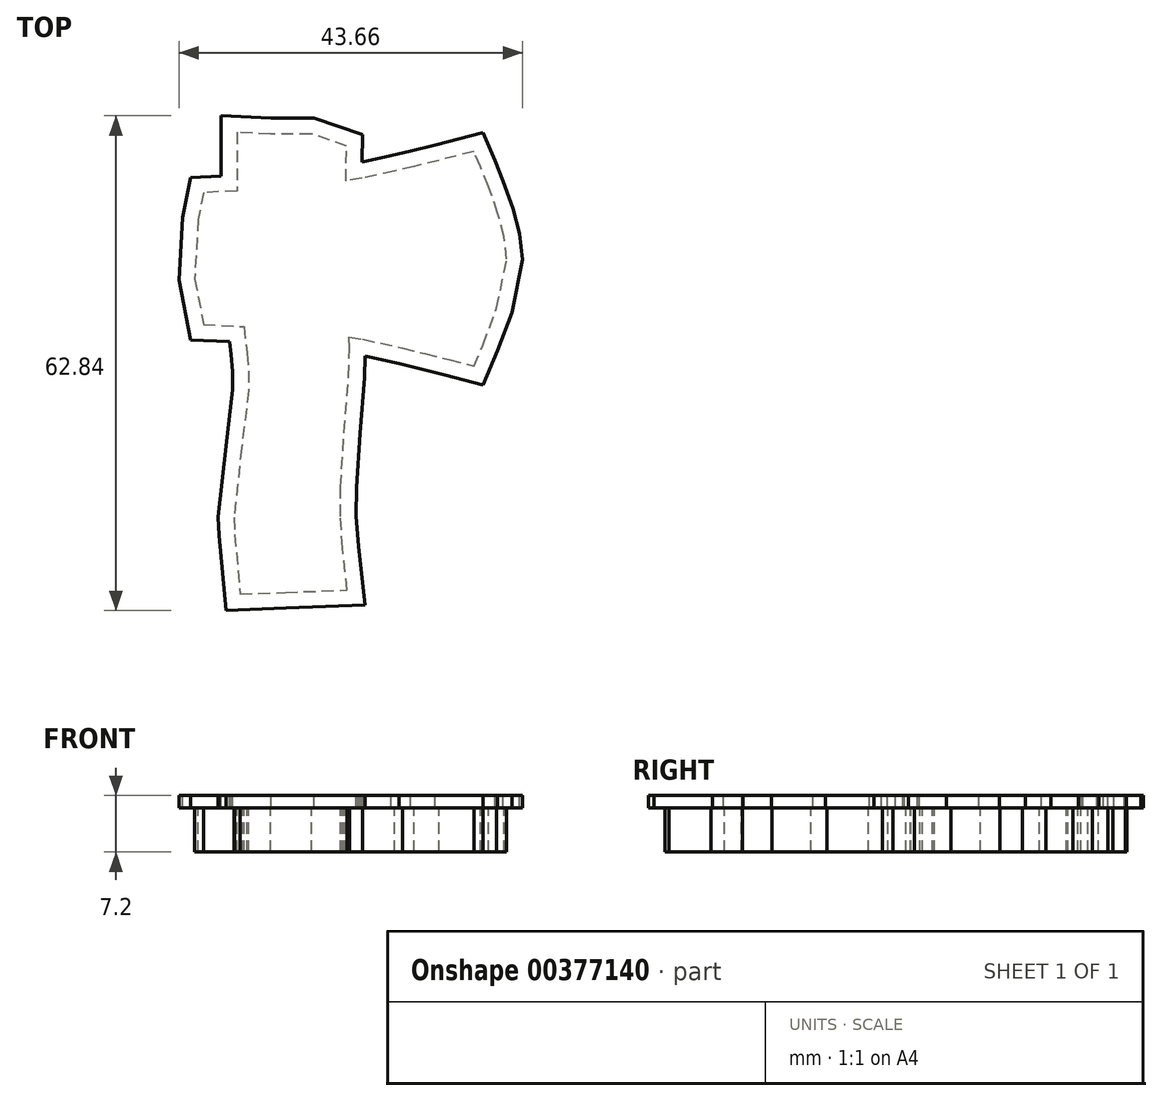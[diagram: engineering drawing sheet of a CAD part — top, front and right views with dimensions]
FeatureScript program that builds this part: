
annotation { "Feature Type Name" : "Feature", "Feature Type Description" : "" }
export const myFeature = defineFeature(function(context is Context, id is Id, definition is map)
    precondition{}
    {
        {
            var Q0;
            Q0=qCreatedBy(makeId("Top.planeOp"),FACE);
            var sketch = newSketch(context, id + "F0", { "sketchPlane" : qUnion([Q0])});
            skLineSegment(sketch, "E0", {"start": v(-5, 5.8) * mm, "end": v(-3.54, 5.88) * mm});
            skLineSegment(sketch, "E1", {"start": v(-3.54, 5.88) * mm, "end": v(-2.42, 5.96) * mm});
            skLineSegment(sketch, "E2", {"start": v(-2.42, 5.96) * mm, "end": v(-1.3, 6.05) * mm});
            skLineSegment(sketch, "E3", {"start": v(-1.3, 6.05) * mm, "end": v(-0.4, 6.16) * mm});
            skLineSegment(sketch, "E4", {"start": v(-0.4, 6.16) * mm, "end": v(0.44, 6.31) * mm});
            skLineSegment(sketch, "E5", {"start": v(0.44, 6.31) * mm, "end": v(1.6, 6.56) * mm});
            skLineSegment(sketch, "E6", {"start": v(1.6, 6.56) * mm, "end": v(2.29, 6.73) * mm});
            skLineSegment(sketch, "E7", {"start": v(2.29, 6.73) * mm, "end": v(3.16, 6.94) * mm});
            skLineSegment(sketch, "E8", {"start": v(3.16, 6.94) * mm, "end": v(4.22, 7.22) * mm});
            skLineSegment(sketch, "E9", {"start": v(4.22, 7.22) * mm, "end": v(4.37, 6.86) * mm});
            skLineSegment(sketch, "E10", {"start": v(4.37, 6.86) * mm, "end": v(4.65, 6.16) * mm});
            skLineSegment(sketch, "E11", {"start": v(4.65, 6.16) * mm, "end": v(4.98, 5.24) * mm});
            skLineSegment(sketch, "E12", {"start": v(4.98, 5.24) * mm, "end": v(5.2, 4.43) * mm});
            skLineSegment(sketch, "E13", {"start": v(5.2, 4.43) * mm, "end": v(5.28, 3.69) * mm});
            skLineSegment(sketch, "E14", {"start": v(5.28, 3.69) * mm, "end": v(4.94, 2) * mm});
            skLineSegment(sketch, "E15", {"start": v(4.94, 2) * mm, "end": v(4.46, 0.74) * mm});
            skLineSegment(sketch, "E16", {"start": v(4.46, 0.74) * mm, "end": v(4.22, 0.16) * mm});
            skLineSegment(sketch, "E17", {"start": v(4.22, 0.16) * mm, "end": v(3.52, 0.34) * mm});
            skLineSegment(sketch, "E18", {"start": v(3.52, 0.34) * mm, "end": v(2.67, 0.56) * mm});
            skLineSegment(sketch, "E19", {"start": v(2.67, 0.56) * mm, "end": v(1.88, 0.75) * mm});
            skLineSegment(sketch, "E20", {"start": v(1.88, 0.75) * mm, "end": v(0.47, 1.06) * mm});
            skLineSegment(sketch, "E21", {"start": v(0.47, 1.06) * mm, "end": v(-0.4, 1.22) * mm});
            skLineSegment(sketch, "E22", {"start": v(-0.4, 1.22) * mm, "end": v(-1.25, 1.33) * mm});
            skLineSegment(sketch, "E23", {"start": v(-1.25, 1.33) * mm, "end": v(-1.92, 1.4) * mm});
            skLineSegment(sketch, "E24", {"start": v(-1.92, 1.4) * mm, "end": v(-2.83, 1.46) * mm});
            skLineSegment(sketch, "E25", {"start": v(-2.83, 1.46) * mm, "end": v(-3.8, 1.52) * mm});
            skLineSegment(sketch, "E26", {"start": v(-3.8, 1.52) * mm, "end": v(-5, 1.58) * mm});
            skLineSegment(sketch, "E27", {"start": v(-5, 1.58) * mm, "end": v(-5.28, 3) * mm});
            skLineSegment(sketch, "E28", {"start": v(-5.28, 3) * mm, "end": v(-5.17, 5.05) * mm});
            skLineSegment(sketch, "E29", {"start": v(-5.17, 5.05) * mm, "end": v(-5, 5.8) * mm});
            skLineSegment(sketch, "E30", {"start": v(-5, 5.8) * mm, "end": v(-5, 5.8) * mm});
            skLineSegment(sketch, "E31", {"start": v(2.86, 0.52) * mm, "end": v(2.86, 1.93) * mm});
            skLineSegment(sketch, "E32", {"start": v(2.86, 1.93) * mm, "end": v(3.16, 3.33) * mm});
            skLineSegment(sketch, "E33", {"start": v(3.16, 3.33) * mm, "end": v(2.86, 4.4) * mm});
            skLineSegment(sketch, "E34", {"start": v(2.86, 4.4) * mm, "end": v(2.86, 6.86) * mm});
            skLineSegment(sketch, "E35", {"start": v(-3.8, 5.87) * mm, "end": v(-3.8, 7.92) * mm});
            skLineSegment(sketch, "E36", {"start": v(-3.8, 7.92) * mm, "end": v(-2.83, 7.87) * mm});
            skLineSegment(sketch, "E37", {"start": v(-2.83, 7.87) * mm, "end": v(-1.42, 7.87) * mm});
            skLineSegment(sketch, "E38", {"start": v(-1.42, 7.87) * mm, "end": v(-0.37, 7.51) * mm});
            skLineSegment(sketch, "E39", {"start": v(-0.37, 7.51) * mm, "end": v(-0.4, 6.16) * mm});
            skLineSegment(sketch, "E40", {"start": v(-0.28, 1.2) * mm, "end": v(-0.27, 0.52) * mm});
            skLineSegment(sketch, "E41", {"start": v(-0.27, 0.52) * mm, "end": v(-0.29, -0.46) * mm});
            skLineSegment(sketch, "E42", {"start": v(-0.29, -0.46) * mm, "end": v(-0.45, -2.42) * mm});
            skLineSegment(sketch, "E43", {"start": v(-0.45, -2.42) * mm, "end": v(-0.58, -4.36) * mm});
            skLineSegment(sketch, "E44", {"start": v(-0.58, -4.36) * mm, "end": v(-0.59, -5.4) * mm});
            skLineSegment(sketch, "E45", {"start": v(-0.59, -5.4) * mm, "end": v(-0.5, -6.53) * mm});
            skLineSegment(sketch, "E46", {"start": v(-0.5, -6.53) * mm, "end": v(-0.37, -7.79) * mm});
            skLineSegment(sketch, "E47", {"start": v(-0.37, -7.79) * mm, "end": v(-2.3, -7.86) * mm});
            skLineSegment(sketch, "E48", {"start": v(-2.3, -7.86) * mm, "end": v(-3.7, -7.92) * mm});
            skLineSegment(sketch, "E49", {"start": v(-3.7, -7.92) * mm, "end": v(-3.87, -6.03) * mm});
            skLineSegment(sketch, "E50", {"start": v(-3.87, -6.03) * mm, "end": v(-3.9, -5.45) * mm});
            skLineSegment(sketch, "E51", {"start": v(-3.9, -5.45) * mm, "end": v(-3.63, -3.01) * mm});
            skLineSegment(sketch, "E52", {"start": v(-3.63, -3.01) * mm, "end": v(-3.38, -0.98) * mm});
            skLineSegment(sketch, "E53", {"start": v(-3.38, -0.98) * mm, "end": v(-3.39, -0.26) * mm});
            skLineSegment(sketch, "E54", {"start": v(-3.39, -0.26) * mm, "end": v(-3.44, 0.38) * mm});
            skLineSegment(sketch, "E55", {"start": v(-3.44, 0.38) * mm, "end": v(-3.57, 1.5) * mm});
            skSolve(sketch);
        }
        {
            var Q0;
            {var subQ8=sQuery(id+"F0.wireOp",EDGE,"E22");Q0=makeQuery(id+"F0.imprint","IMPRINT",FACE,{"disambiguationData":[TD([[makeQuery(id+"F0.imprint","IMPRINT",EDGE,{"derivedFrom":subQ8}),1.0]])]});}
            var Q1;
            {var subQ1=sQuery(id+"F0.wireOp",EDGE,"E1");Q1=makeQuery(id+"F0.imprint","IMPRINT",FACE,{"disambiguationData":[TD([[makeQuery(id+"F0.imprint","IMPRINT",EDGE,{"derivedFrom":subQ1}),-1.0]])]});}
            var Q2;
            {var subQ0=sQuery(id+"F0.wireOp",EDGE,"E1");Q2=makeQuery(id+"F0.imprint","IMPRINT",FACE,{"disambiguationData":[TD([[makeQuery(id+"F0.imprint","IMPRINT",EDGE,{"derivedFrom":subQ0}),1.0]])]});}
            extrude(context, id + "F1", {"entities" : qUnion([Q0, Q1, Q2]), "depth" : 2 * mm});
        }
        {
            var Q0;
            Q0=makeQuery(id+"F1.opExtrude","SWEPT_BODY",BODY,{"disambiguationData":[OSD([sQuery(id+"F0.wireOp",EDGE,"E0"),sQuery(id+"F0.wireOp",EDGE,"E4"),sQuery(id+"F0.wireOp",EDGE,"E5"),sQuery(id+"F0.wireOp",EDGE,"E6"),sQuery(id+"F0.wireOp",EDGE,"E7"),sQuery(id+"F0.wireOp",EDGE,"E8"),sQuery(id+"F0.wireOp",EDGE,"E9"),sQuery(id+"F0.wireOp",EDGE,"E10"),sQuery(id+"F0.wireOp",EDGE,"E11"),sQuery(id+"F0.wireOp",EDGE,"E12"),sQuery(id+"F0.wireOp",EDGE,"E13"),sQuery(id+"F0.wireOp",EDGE,"E14"),sQuery(id+"F0.wireOp",EDGE,"E15"),sQuery(id+"F0.wireOp",EDGE,"E16"),sQuery(id+"F0.wireOp",EDGE,"E17"),sQuery(id+"F0.wireOp",EDGE,"E18"),sQuery(id+"F0.wireOp",EDGE,"E19"),sQuery(id+"F0.wireOp",EDGE,"E20"),sQuery(id+"F0.wireOp",EDGE,"E21"),sQuery(id+"F0.wireOp",EDGE,"E25"),sQuery(id+"F0.wireOp",EDGE,"E26"),sQuery(id+"F0.wireOp",EDGE,"E27"),sQuery(id+"F0.wireOp",EDGE,"E28"),sQuery(id+"F0.wireOp",EDGE,"E29"),sQuery(id+"F0.wireOp",EDGE,"E35"),sQuery(id+"F0.wireOp",EDGE,"E36"),sQuery(id+"F0.wireOp",EDGE,"E37"),sQuery(id+"F0.wireOp",EDGE,"E38"),sQuery(id+"F0.wireOp",EDGE,"E39"),sQuery(id+"F0.wireOp",EDGE,"E40"),sQuery(id+"F0.wireOp",EDGE,"E41"),sQuery(id+"F0.wireOp",EDGE,"E42"),sQuery(id+"F0.wireOp",EDGE,"E43"),sQuery(id+"F0.wireOp",EDGE,"E44"),sQuery(id+"F0.wireOp",EDGE,"E45"),sQuery(id+"F0.wireOp",EDGE,"E46"),sQuery(id+"F0.wireOp",EDGE,"E47"),sQuery(id+"F0.wireOp",EDGE,"E48"),sQuery(id+"F0.wireOp",EDGE,"E49"),sQuery(id+"F0.wireOp",EDGE,"E50"),sQuery(id+"F0.wireOp",EDGE,"E51"),sQuery(id+"F0.wireOp",EDGE,"E52"),sQuery(id+"F0.wireOp",EDGE,"E53"),sQuery(id+"F0.wireOp",EDGE,"E54"),sQuery(id+"F0.wireOp",EDGE,"E55")])]});
            var Q1;
            Q1=qCreatedBy(makeId("Origin.pointOp"),VERTEX);
            transform(context, id + "F2", {"entities" : qUnion([Q0]), "transformType" : TransformType.SCALE_UNIFORMLY, "scale" : 3.6, "scalePoint" : qUnion([Q1]), "makeCopy" : false});
        }
        {
            var Q0;
            Q0=makeQuery(id+"F1.opExtrude","CAP_FACE",FACE,{"disambiguationData":[OSD([sQuery(id+"F0.wireOp",EDGE,"E0"),sQuery(id+"F0.wireOp",EDGE,"E4"),sQuery(id+"F0.wireOp",EDGE,"E5"),sQuery(id+"F0.wireOp",EDGE,"E6"),sQuery(id+"F0.wireOp",EDGE,"E7"),sQuery(id+"F0.wireOp",EDGE,"E8"),sQuery(id+"F0.wireOp",EDGE,"E9"),sQuery(id+"F0.wireOp",EDGE,"E10"),sQuery(id+"F0.wireOp",EDGE,"E11"),sQuery(id+"F0.wireOp",EDGE,"E12"),sQuery(id+"F0.wireOp",EDGE,"E13"),sQuery(id+"F0.wireOp",EDGE,"E14"),sQuery(id+"F0.wireOp",EDGE,"E15"),sQuery(id+"F0.wireOp",EDGE,"E16"),sQuery(id+"F0.wireOp",EDGE,"E17"),sQuery(id+"F0.wireOp",EDGE,"E18"),sQuery(id+"F0.wireOp",EDGE,"E19"),sQuery(id+"F0.wireOp",EDGE,"E20"),sQuery(id+"F0.wireOp",EDGE,"E21"),sQuery(id+"F0.wireOp",EDGE,"E25"),sQuery(id+"F0.wireOp",EDGE,"E26"),sQuery(id+"F0.wireOp",EDGE,"E27"),sQuery(id+"F0.wireOp",EDGE,"E28"),sQuery(id+"F0.wireOp",EDGE,"E29"),sQuery(id+"F0.wireOp",EDGE,"E35"),sQuery(id+"F0.wireOp",EDGE,"E36"),sQuery(id+"F0.wireOp",EDGE,"E37"),sQuery(id+"F0.wireOp",EDGE,"E38"),sQuery(id+"F0.wireOp",EDGE,"E39"),sQuery(id+"F0.wireOp",EDGE,"E40"),sQuery(id+"F0.wireOp",EDGE,"E41"),sQuery(id+"F0.wireOp",EDGE,"E42"),sQuery(id+"F0.wireOp",EDGE,"E43"),sQuery(id+"F0.wireOp",EDGE,"E44"),sQuery(id+"F0.wireOp",EDGE,"E45"),sQuery(id+"F0.wireOp",EDGE,"E46"),sQuery(id+"F0.wireOp",EDGE,"E47"),sQuery(id+"F0.wireOp",EDGE,"E48"),sQuery(id+"F0.wireOp",EDGE,"E49"),sQuery(id+"F0.wireOp",EDGE,"E50"),sQuery(id+"F0.wireOp",EDGE,"E51"),sQuery(id+"F0.wireOp",EDGE,"E52"),sQuery(id+"F0.wireOp",EDGE,"E53"),sQuery(id+"F0.wireOp",EDGE,"E54"),sQuery(id+"F0.wireOp",EDGE,"E55")])],"isStart":false});
            var sketch = newSketch(context, id + "F3", { "sketchPlane" : qUnion([Q0])});
            skLineSegment(sketch, "E56.0", {"start": v(-18.7, 4.9) * mm, "end": v(-13.7, 4.66) * mm});
            skLineSegment(sketch, "E56.1", {"start": v(-19.81, 10.72) * mm, "end": v(-18.7, 4.9) * mm});
            skLineSegment(sketch, "E56.2", {"start": v(-19.4, 18.27) * mm, "end": v(-19.81, 10.72) * mm});
            skLineSegment(sketch, "E56.3", {"start": v(-18.69, 21.68) * mm, "end": v(-19.4, 18.27) * mm});
            skLineSegment(sketch, "E56.4", {"start": v(-14.46, 21.9) * mm, "end": v(-18.69, 21.68) * mm});
            skLineSegment(sketch, "E56.5", {"start": v(-14.46, 29.34) * mm, "end": v(-14.46, 21.9) * mm});
            skLineSegment(sketch, "E56.6", {"start": v(-10.18, 29.13) * mm, "end": v(-14.46, 29.34) * mm});
            skLineSegment(sketch, "E56.7", {"start": v(-4.99, 29.13) * mm, "end": v(-10.18, 29.13) * mm});
            skLineSegment(sketch, "E56.8", {"start": v(-0.52, 27.6) * mm, "end": v(-4.99, 29.13) * mm});
            skLineSegment(sketch, "E56.9", {"start": v(-0.6, 23.14) * mm, "end": v(-0.52, 27.6) * mm});
            skLineSegment(sketch, "E56.10", {"start": v(1.42, 23.5) * mm, "end": v(-0.6, 23.14) * mm});
            skLineSegment(sketch, "E56.11", {"start": v(-13.7, 4.66) * mm, "end": v(-13.56, 4.65) * mm});
            skLineSegment(sketch, "E56.12", {"start": v(5.56, 24.4) * mm, "end": v(1.42, 23.5) * mm});
            skLineSegment(sketch, "E56.13", {"start": v(8.04, 25) * mm, "end": v(5.56, 24.4) * mm});
            skLineSegment(sketch, "E56.14", {"start": v(11.2, 25.77) * mm, "end": v(8.04, 25) * mm});
            skLineSegment(sketch, "E56.15", {"start": v(15.64, 26.92) * mm, "end": v(11.2, 25.77) * mm});
            skLineSegment(sketch, "E56.16", {"start": v(16.48, 25) * mm, "end": v(15.64, 26.92) * mm});
            skLineSegment(sketch, "E56.17", {"start": v(17.5, 22.47) * mm, "end": v(16.48, 25) * mm});
            skLineSegment(sketch, "E56.18", {"start": v(18.68, 19.1) * mm, "end": v(17.5, 22.47) * mm});
            skLineSegment(sketch, "E56.19", {"start": v(19.47, 16.1) * mm, "end": v(18.68, 19.1) * mm});
            skLineSegment(sketch, "E56.20", {"start": v(19.82, 13.24) * mm, "end": v(19.47, 16.1) * mm});
            skLineSegment(sketch, "E56.21", {"start": v(18.54, 7) * mm, "end": v(19.82, 13.24) * mm});
            skLineSegment(sketch, "E56.22", {"start": v(16.82, 2.35) * mm, "end": v(18.54, 7) * mm});
            skLineSegment(sketch, "E56.23", {"start": v(-0.43, -28.8) * mm, "end": v(-1.03, -23.45) * mm});
            skLineSegment(sketch, "E56.24", {"start": v(-8.28, -29.1) * mm, "end": v(-0.43, -28.8) * mm});
            skLineSegment(sketch, "E56.25", {"start": v(-14.03, -29.33) * mm, "end": v(-8.28, -29.1) * mm});
            skLineSegment(sketch, "E56.26", {"start": v(-14.73, -21.77) * mm, "end": v(-14.03, -29.33) * mm});
            skLineSegment(sketch, "E56.27", {"start": v(-14.81, -19.6) * mm, "end": v(-14.73, -21.77) * mm});
            skLineSegment(sketch, "E56.28", {"start": v(-13.86, -10.75) * mm, "end": v(-14.81, -19.6) * mm});
            skLineSegment(sketch, "E56.29", {"start": v(-13.56, 4.65) * mm, "end": v(-13.19, 1.3) * mm});
            skLineSegment(sketch, "E56.30", {"start": v(-13.19, 1.3) * mm, "end": v(-13, -0.98) * mm});
            skLineSegment(sketch, "E56.31", {"start": v(-13, -0.98) * mm, "end": v(-12.98, -3.47) * mm});
            skLineSegment(sketch, "E56.32", {"start": v(-12.98, -3.47) * mm, "end": v(-13.86, -10.75) * mm});
            skLineSegment(sketch, "E56.33", {"start": v(-1.03, -23.45) * mm, "end": v(-1.31, -19.45) * mm});
            skLineSegment(sketch, "E56.34", {"start": v(-1.31, -19.45) * mm, "end": v(-1.28, -15.72) * mm});
            skLineSegment(sketch, "E56.35", {"start": v(-1.28, -15.72) * mm, "end": v(-0.82, -8.77) * mm});
            skLineSegment(sketch, "E56.36", {"start": v(-0.82, -8.77) * mm, "end": v(-0.24, -1.7) * mm});
            skLineSegment(sketch, "E56.37", {"start": v(-0.24, -1.7) * mm, "end": v(-0.17, 1.86) * mm});
            skLineSegment(sketch, "E56.38", {"start": v(-0.17, 1.86) * mm, "end": v(-0.18, 3.36) * mm});
            skLineSegment(sketch, "E56.39", {"start": v(-0.18, 3.36) * mm, "end": v(1.54, 3.05) * mm});
            skLineSegment(sketch, "E56.40", {"start": v(1.54, 3.05) * mm, "end": v(6.6, 1.92) * mm});
            skLineSegment(sketch, "E56.41", {"start": v(6.6, 1.92) * mm, "end": v(9.43, 1.23) * mm});
            skLineSegment(sketch, "E56.42", {"start": v(9.43, 1.23) * mm, "end": v(12.47, 0.46) * mm});
            skLineSegment(sketch, "E56.43", {"start": v(12.47, 0.46) * mm, "end": v(15.64, -0.37) * mm});
            skLineSegment(sketch, "E56.44", {"start": v(15.64, -0.37) * mm, "end": v(16.82, 2.35) * mm});
            skSolve(sketch);
        }
        {
            var Q0;
            Q0=makeQuery(id+"F3.imprint","IMPRINT",FACE,{"disambiguationData":[TD([[makeQuery(id+"F3.imprint","IMPRINT",EDGE,{"derivedFrom":sQuery(id+"F3.wireOp",EDGE,"E56.0")}),1.0]])]});
            var Q1;
            Q1=makeQuery(id+"F1.opExtrude","CAP_FACE",FACE,{"disambiguationData":[OSD([sQuery(id+"F0.wireOp",EDGE,"E0"),sQuery(id+"F0.wireOp",EDGE,"E4"),sQuery(id+"F0.wireOp",EDGE,"E5"),sQuery(id+"F0.wireOp",EDGE,"E6"),sQuery(id+"F0.wireOp",EDGE,"E7"),sQuery(id+"F0.wireOp",EDGE,"E8"),sQuery(id+"F0.wireOp",EDGE,"E9"),sQuery(id+"F0.wireOp",EDGE,"E10"),sQuery(id+"F0.wireOp",EDGE,"E11"),sQuery(id+"F0.wireOp",EDGE,"E12"),sQuery(id+"F0.wireOp",EDGE,"E13"),sQuery(id+"F0.wireOp",EDGE,"E14"),sQuery(id+"F0.wireOp",EDGE,"E15"),sQuery(id+"F0.wireOp",EDGE,"E16"),sQuery(id+"F0.wireOp",EDGE,"E17"),sQuery(id+"F0.wireOp",EDGE,"E18"),sQuery(id+"F0.wireOp",EDGE,"E19"),sQuery(id+"F0.wireOp",EDGE,"E20"),sQuery(id+"F0.wireOp",EDGE,"E21"),sQuery(id+"F0.wireOp",EDGE,"E25"),sQuery(id+"F0.wireOp",EDGE,"E26"),sQuery(id+"F0.wireOp",EDGE,"E27"),sQuery(id+"F0.wireOp",EDGE,"E28"),sQuery(id+"F0.wireOp",EDGE,"E29"),sQuery(id+"F0.wireOp",EDGE,"E35"),sQuery(id+"F0.wireOp",EDGE,"E36"),sQuery(id+"F0.wireOp",EDGE,"E37"),sQuery(id+"F0.wireOp",EDGE,"E38"),sQuery(id+"F0.wireOp",EDGE,"E39"),sQuery(id+"F0.wireOp",EDGE,"E40"),sQuery(id+"F0.wireOp",EDGE,"E41"),sQuery(id+"F0.wireOp",EDGE,"E42"),sQuery(id+"F0.wireOp",EDGE,"E43"),sQuery(id+"F0.wireOp",EDGE,"E44"),sQuery(id+"F0.wireOp",EDGE,"E45"),sQuery(id+"F0.wireOp",EDGE,"E46"),sQuery(id+"F0.wireOp",EDGE,"E47"),sQuery(id+"F0.wireOp",EDGE,"E48"),sQuery(id+"F0.wireOp",EDGE,"E49"),sQuery(id+"F0.wireOp",EDGE,"E50"),sQuery(id+"F0.wireOp",EDGE,"E51"),sQuery(id+"F0.wireOp",EDGE,"E52"),sQuery(id+"F0.wireOp",EDGE,"E53"),sQuery(id+"F0.wireOp",EDGE,"E54"),sQuery(id+"F0.wireOp",EDGE,"E55")])],"isStart":true});
            extrude(context, id + "F4", {"entities" : qUnion([Q0]), "endBound" : BoundingType.UP_TO_SURFACE, "oppositeDirection" : true, "endBoundEntityFace" : qUnion([Q1]), "depth" : 5 * mm});
        }
        {
            var Q0;
            Q0=makeQuery(id+"F4.opExtrude","CAP_FACE",FACE,{"disambiguationData":[OSD([sQuery(id+"F0.wireOp",EDGE,"E0"),sQuery(id+"F0.wireOp",EDGE,"E4"),sQuery(id+"F0.wireOp",EDGE,"E5"),sQuery(id+"F0.wireOp",EDGE,"E6"),sQuery(id+"F0.wireOp",EDGE,"E7"),sQuery(id+"F0.wireOp",EDGE,"E8"),sQuery(id+"F0.wireOp",EDGE,"E9"),sQuery(id+"F0.wireOp",EDGE,"E10"),sQuery(id+"F0.wireOp",EDGE,"E11"),sQuery(id+"F0.wireOp",EDGE,"E12"),sQuery(id+"F0.wireOp",EDGE,"E13"),sQuery(id+"F0.wireOp",EDGE,"E14"),sQuery(id+"F0.wireOp",EDGE,"E15"),sQuery(id+"F0.wireOp",EDGE,"E16"),sQuery(id+"F0.wireOp",EDGE,"E17"),sQuery(id+"F0.wireOp",EDGE,"E18"),sQuery(id+"F0.wireOp",EDGE,"E19"),sQuery(id+"F0.wireOp",EDGE,"E20"),sQuery(id+"F0.wireOp",EDGE,"E21"),sQuery(id+"F0.wireOp",EDGE,"E25"),sQuery(id+"F0.wireOp",EDGE,"E26"),sQuery(id+"F0.wireOp",EDGE,"E27"),sQuery(id+"F0.wireOp",EDGE,"E28"),sQuery(id+"F0.wireOp",EDGE,"E29"),sQuery(id+"F0.wireOp",EDGE,"E35"),sQuery(id+"F0.wireOp",EDGE,"E36"),sQuery(id+"F0.wireOp",EDGE,"E37"),sQuery(id+"F0.wireOp",EDGE,"E38"),sQuery(id+"F0.wireOp",EDGE,"E39"),sQuery(id+"F0.wireOp",EDGE,"E40"),sQuery(id+"F0.wireOp",EDGE,"E41"),sQuery(id+"F0.wireOp",EDGE,"E42"),sQuery(id+"F0.wireOp",EDGE,"E43"),sQuery(id+"F0.wireOp",EDGE,"E44"),sQuery(id+"F0.wireOp",EDGE,"E45"),sQuery(id+"F0.wireOp",EDGE,"E46"),sQuery(id+"F0.wireOp",EDGE,"E47"),sQuery(id+"F0.wireOp",EDGE,"E48"),sQuery(id+"F0.wireOp",EDGE,"E49"),sQuery(id+"F0.wireOp",EDGE,"E50"),sQuery(id+"F0.wireOp",EDGE,"E51"),sQuery(id+"F0.wireOp",EDGE,"E52"),sQuery(id+"F0.wireOp",EDGE,"E53"),sQuery(id+"F0.wireOp",EDGE,"E54"),sQuery(id+"F0.wireOp",EDGE,"E55"),sQuery(id+"F3.wireOp",EDGE,"E56.0"),sQuery(id+"F3.wireOp",EDGE,"E56.1"),sQuery(id+"F3.wireOp",EDGE,"E56.2"),sQuery(id+"F3.wireOp",EDGE,"E56.3"),sQuery(id+"F3.wireOp",EDGE,"E56.4"),sQuery(id+"F3.wireOp",EDGE,"E56.5"),sQuery(id+"F3.wireOp",EDGE,"E56.6"),sQuery(id+"F3.wireOp",EDGE,"E56.7"),sQuery(id+"F3.wireOp",EDGE,"E56.8"),sQuery(id+"F3.wireOp",EDGE,"E56.9"),sQuery(id+"F3.wireOp",EDGE,"E56.10"),sQuery(id+"F3.wireOp",EDGE,"E56.11"),sQuery(id+"F3.wireOp",EDGE,"E56.12"),sQuery(id+"F3.wireOp",EDGE,"E56.13"),sQuery(id+"F3.wireOp",EDGE,"E56.14"),sQuery(id+"F3.wireOp",EDGE,"E56.15"),sQuery(id+"F3.wireOp",EDGE,"E56.16"),sQuery(id+"F3.wireOp",EDGE,"E56.17"),sQuery(id+"F3.wireOp",EDGE,"E56.18"),sQuery(id+"F3.wireOp",EDGE,"E56.19"),sQuery(id+"F3.wireOp",EDGE,"E56.20"),sQuery(id+"F3.wireOp",EDGE,"E56.21"),sQuery(id+"F3.wireOp",EDGE,"E56.22"),sQuery(id+"F3.wireOp",EDGE,"E56.23"),sQuery(id+"F3.wireOp",EDGE,"E56.24"),sQuery(id+"F3.wireOp",EDGE,"E56.25"),sQuery(id+"F3.wireOp",EDGE,"E56.26"),sQuery(id+"F3.wireOp",EDGE,"E56.27"),sQuery(id+"F3.wireOp",EDGE,"E56.28"),sQuery(id+"F3.wireOp",EDGE,"E56.29"),sQuery(id+"F3.wireOp",EDGE,"E56.30"),sQuery(id+"F3.wireOp",EDGE,"E56.31"),sQuery(id+"F3.wireOp",EDGE,"E56.32"),sQuery(id+"F3.wireOp",EDGE,"E56.33"),sQuery(id+"F3.wireOp",EDGE,"E56.34"),sQuery(id+"F3.wireOp",EDGE,"E56.35"),sQuery(id+"F3.wireOp",EDGE,"E56.36"),sQuery(id+"F3.wireOp",EDGE,"E56.37"),sQuery(id+"F3.wireOp",EDGE,"E56.38"),sQuery(id+"F3.wireOp",EDGE,"E56.39"),sQuery(id+"F3.wireOp",EDGE,"E56.40"),sQuery(id+"F3.wireOp",EDGE,"E56.41"),sQuery(id+"F3.wireOp",EDGE,"E56.42"),sQuery(id+"F3.wireOp",EDGE,"E56.43"),sQuery(id+"F3.wireOp",EDGE,"E56.44")])],"isStart":true});
            var sketch = newSketch(context, id + "F5", { "sketchPlane" : qUnion([Q0])});
            skLineSegment(sketch, "E57", {"start": v(9.8, 24.6) * mm, "end": v(9.8, 13.66) * mm});
            skLineSegment(sketch, "E58", {"start": v(9.8, 13.66) * mm, "end": v(8.23, 11.38) * mm});
            skLineSegment(sketch, "E59", {"start": v(8.23, 11.38) * mm, "end": v(9.73, 7) * mm});
            skLineSegment(sketch, "E60", {"start": v(9.73, 7) * mm, "end": v(9.62, 2.01) * mm});
            skLineSegment(sketch, "E61.0", {"start": v(8.23, 24.22) * mm, "end": v(11.39, 25) * mm});
            skLineSegment(sketch, "E62.0", {"start": v(12.67, 1.24) * mm, "end": v(9.62, 2.01) * mm});
            skLineSegment(sketch, "E63.0", {"start": v(9.62, 2.01) * mm, "end": v(6.77, 2.7) * mm});
            skLineSegment(sketch, "E64.0", {"start": v(8.13, 6.76) * mm, "end": v(8.01, 1.8) * mm});
            skLineSegment(sketch, "E64.1", {"start": v(6.45, 11.63) * mm, "end": v(8.13, 6.76) * mm});
            skLineSegment(sketch, "E64.2", {"start": v(8.2, 14.16) * mm, "end": v(6.45, 11.63) * mm});
            skLineSegment(sketch, "E64.3", {"start": v(8.2, 24.6) * mm, "end": v(8.2, 14.16) * mm});
            skSolve(sketch);
        }
        {
            var Q0;
            {var subQ5=sQuery(id+"F5.wireOp",EDGE,"E57");Q0=makeQuery(id+"F5.imprint","IMPRINT",FACE,{"disambiguationData":[TD([[makeQuery(id+"F5.imprint","IMPRINT",EDGE,{"derivedFrom":subQ5}),-1.0]])]});}
            extrude(context, id + "F6", {"entities" : qUnion([Q0]), "operationType" : NewBodyOperationType.ADD, "oppositeDirection" : true, "depth" : 5 * mm});
        }
        {
            var Q0;
            Q0=makeQuery(id+"F6.boolean.opBoolean","MERGE",FACE,{"derivedFrom":[makeQuery(id+"F4.opExtrude","CAP_FACE",FACE,{"disambiguationData":[OSD([sQuery(id+"F0.wireOp",EDGE,"E0"),sQuery(id+"F0.wireOp",EDGE,"E4"),sQuery(id+"F0.wireOp",EDGE,"E5"),sQuery(id+"F0.wireOp",EDGE,"E6"),sQuery(id+"F0.wireOp",EDGE,"E7"),sQuery(id+"F0.wireOp",EDGE,"E8"),sQuery(id+"F0.wireOp",EDGE,"E9"),sQuery(id+"F0.wireOp",EDGE,"E10"),sQuery(id+"F0.wireOp",EDGE,"E11"),sQuery(id+"F0.wireOp",EDGE,"E12"),sQuery(id+"F0.wireOp",EDGE,"E13"),sQuery(id+"F0.wireOp",EDGE,"E14"),sQuery(id+"F0.wireOp",EDGE,"E15"),sQuery(id+"F0.wireOp",EDGE,"E16"),sQuery(id+"F0.wireOp",EDGE,"E17"),sQuery(id+"F0.wireOp",EDGE,"E18"),sQuery(id+"F0.wireOp",EDGE,"E19"),sQuery(id+"F0.wireOp",EDGE,"E20"),sQuery(id+"F0.wireOp",EDGE,"E21"),sQuery(id+"F0.wireOp",EDGE,"E25"),sQuery(id+"F0.wireOp",EDGE,"E26"),sQuery(id+"F0.wireOp",EDGE,"E27"),sQuery(id+"F0.wireOp",EDGE,"E28"),sQuery(id+"F0.wireOp",EDGE,"E29"),sQuery(id+"F0.wireOp",EDGE,"E35"),sQuery(id+"F0.wireOp",EDGE,"E36"),sQuery(id+"F0.wireOp",EDGE,"E37"),sQuery(id+"F0.wireOp",EDGE,"E38"),sQuery(id+"F0.wireOp",EDGE,"E39"),sQuery(id+"F0.wireOp",EDGE,"E40"),sQuery(id+"F0.wireOp",EDGE,"E41"),sQuery(id+"F0.wireOp",EDGE,"E42"),sQuery(id+"F0.wireOp",EDGE,"E43"),sQuery(id+"F0.wireOp",EDGE,"E44"),sQuery(id+"F0.wireOp",EDGE,"E45"),sQuery(id+"F0.wireOp",EDGE,"E46"),sQuery(id+"F0.wireOp",EDGE,"E47"),sQuery(id+"F0.wireOp",EDGE,"E48"),sQuery(id+"F0.wireOp",EDGE,"E49"),sQuery(id+"F0.wireOp",EDGE,"E50"),sQuery(id+"F0.wireOp",EDGE,"E51"),sQuery(id+"F0.wireOp",EDGE,"E52"),sQuery(id+"F0.wireOp",EDGE,"E53"),sQuery(id+"F0.wireOp",EDGE,"E54"),sQuery(id+"F0.wireOp",EDGE,"E55"),sQuery(id+"F3.wireOp",EDGE,"E56.0"),sQuery(id+"F3.wireOp",EDGE,"E56.1"),sQuery(id+"F3.wireOp",EDGE,"E56.2"),sQuery(id+"F3.wireOp",EDGE,"E56.3"),sQuery(id+"F3.wireOp",EDGE,"E56.4"),sQuery(id+"F3.wireOp",EDGE,"E56.5"),sQuery(id+"F3.wireOp",EDGE,"E56.6"),sQuery(id+"F3.wireOp",EDGE,"E56.7"),sQuery(id+"F3.wireOp",EDGE,"E56.8"),sQuery(id+"F3.wireOp",EDGE,"E56.9"),sQuery(id+"F3.wireOp",EDGE,"E56.10"),sQuery(id+"F3.wireOp",EDGE,"E56.11"),sQuery(id+"F3.wireOp",EDGE,"E56.12"),sQuery(id+"F3.wireOp",EDGE,"E56.13"),sQuery(id+"F3.wireOp",EDGE,"E56.14"),sQuery(id+"F3.wireOp",EDGE,"E56.15"),sQuery(id+"F3.wireOp",EDGE,"E56.16"),sQuery(id+"F3.wireOp",EDGE,"E56.17"),sQuery(id+"F3.wireOp",EDGE,"E56.18"),sQuery(id+"F3.wireOp",EDGE,"E56.19"),sQuery(id+"F3.wireOp",EDGE,"E56.20"),sQuery(id+"F3.wireOp",EDGE,"E56.21"),sQuery(id+"F3.wireOp",EDGE,"E56.22"),sQuery(id+"F3.wireOp",EDGE,"E56.23"),sQuery(id+"F3.wireOp",EDGE,"E56.24"),sQuery(id+"F3.wireOp",EDGE,"E56.25"),sQuery(id+"F3.wireOp",EDGE,"E56.26"),sQuery(id+"F3.wireOp",EDGE,"E56.27"),sQuery(id+"F3.wireOp",EDGE,"E56.28"),sQuery(id+"F3.wireOp",EDGE,"E56.29"),sQuery(id+"F3.wireOp",EDGE,"E56.30"),sQuery(id+"F3.wireOp",EDGE,"E56.31"),sQuery(id+"F3.wireOp",EDGE,"E56.32"),sQuery(id+"F3.wireOp",EDGE,"E56.33"),sQuery(id+"F3.wireOp",EDGE,"E56.34"),sQuery(id+"F3.wireOp",EDGE,"E56.35"),sQuery(id+"F3.wireOp",EDGE,"E56.36"),sQuery(id+"F3.wireOp",EDGE,"E56.37"),sQuery(id+"F3.wireOp",EDGE,"E56.38"),sQuery(id+"F3.wireOp",EDGE,"E56.39"),sQuery(id+"F3.wireOp",EDGE,"E56.40"),sQuery(id+"F3.wireOp",EDGE,"E56.41"),sQuery(id+"F3.wireOp",EDGE,"E56.42"),sQuery(id+"F3.wireOp",EDGE,"E56.43"),sQuery(id+"F3.wireOp",EDGE,"E56.44")])],"isStart":true}),makeQuery(id+"F6.opExtrude","CAP_FACE",FACE,{"disambiguationData":[OSD([sQuery(id+"F5.wireOp",EDGE,"E57"),sQuery(id+"F5.wireOp",EDGE,"E58"),sQuery(id+"F5.wireOp",EDGE,"E59"),sQuery(id+"F5.wireOp",EDGE,"E60"),sQuery(id+"F5.wireOp",EDGE,"E61.0"),sQuery(id+"F5.wireOp",EDGE,"E63.0"),sQuery(id+"F5.wireOp",EDGE,"E64.0"),sQuery(id+"F5.wireOp",EDGE,"E64.1"),sQuery(id+"F5.wireOp",EDGE,"E64.2"),sQuery(id+"F5.wireOp",EDGE,"E64.3")])],"isStart":true})]});
            var sketch = newSketch(context, id + "F7", { "sketchPlane" : qUnion([Q0])});
            skLineSegment(sketch, "E65.0.0", {"start": v(-0.24, -1.7) * mm, "end": v(-0.17, 1.86) * mm});
            skLineSegment(sketch, "E65.0.1", {"start": v(-0.17, 1.86) * mm, "end": v(-0.18, 3.36) * mm});
            skLineSegment(sketch, "E65.0.2", {"start": v(-0.18, 3.36) * mm, "end": v(1.54, 3.05) * mm});
            skLineSegment(sketch, "E65.0.3", {"start": v(1.54, 3.05) * mm, "end": v(6.6, 1.92) * mm});
            skLineSegment(sketch, "E65.0.4", {"start": v(6.6, 1.92) * mm, "end": v(9.43, 1.23) * mm});
            skLineSegment(sketch, "E65.0.5", {"start": v(9.43, 1.23) * mm, "end": v(12.47, 0.46) * mm});
            skLineSegment(sketch, "E65.0.6", {"start": v(12.47, 0.46) * mm, "end": v(15.64, -0.37) * mm});
            skLineSegment(sketch, "E65.0.7", {"start": v(15.64, -0.37) * mm, "end": v(16.82, 2.35) * mm});
            skLineSegment(sketch, "E65.0.8", {"start": v(16.82, 2.35) * mm, "end": v(18.54, 7) * mm});
            skLineSegment(sketch, "E65.0.9", {"start": v(18.54, 7) * mm, "end": v(19.82, 13.24) * mm});
            skLineSegment(sketch, "E65.0.10", {"start": v(19.82, 13.24) * mm, "end": v(19.47, 16.1) * mm});
            skLineSegment(sketch, "E65.0.11", {"start": v(19.47, 16.1) * mm, "end": v(18.68, 19.1) * mm});
            skLineSegment(sketch, "E65.0.12", {"start": v(18.68, 19.1) * mm, "end": v(17.5, 22.47) * mm});
            skLineSegment(sketch, "E65.0.13", {"start": v(17.5, 22.47) * mm, "end": v(16.48, 25) * mm});
            skLineSegment(sketch, "E65.0.14", {"start": v(16.48, 25) * mm, "end": v(15.64, 26.92) * mm});
            skLineSegment(sketch, "E65.0.15", {"start": v(15.64, 26.92) * mm, "end": v(11.2, 25.77) * mm});
            skLineSegment(sketch, "E65.0.16", {"start": v(11.2, 25.77) * mm, "end": v(8.04, 25) * mm});
            skLineSegment(sketch, "E65.0.17", {"start": v(8.04, 25) * mm, "end": v(5.56, 24.4) * mm});
            skLineSegment(sketch, "E65.0.18", {"start": v(5.56, 24.4) * mm, "end": v(1.42, 23.5) * mm});
            skLineSegment(sketch, "E65.0.19", {"start": v(1.42, 23.5) * mm, "end": v(-0.6, 23.14) * mm});
            skLineSegment(sketch, "E65.0.20", {"start": v(-0.6, 23.14) * mm, "end": v(-0.52, 27.6) * mm});
            skLineSegment(sketch, "E65.0.21", {"start": v(-0.52, 27.6) * mm, "end": v(-4.99, 29.13) * mm});
            skLineSegment(sketch, "E65.0.22", {"start": v(-4.99, 29.13) * mm, "end": v(-10.18, 29.13) * mm});
            skLineSegment(sketch, "E65.0.23", {"start": v(-10.18, 29.13) * mm, "end": v(-14.46, 29.34) * mm});
            skLineSegment(sketch, "E65.0.24", {"start": v(-14.46, 29.34) * mm, "end": v(-14.46, 21.9) * mm});
            skLineSegment(sketch, "E65.0.25", {"start": v(-14.46, 21.9) * mm, "end": v(-18.69, 21.68) * mm});
            skLineSegment(sketch, "E65.0.26", {"start": v(-18.69, 21.68) * mm, "end": v(-19.4, 18.27) * mm});
            skLineSegment(sketch, "E65.0.27", {"start": v(-19.4, 18.27) * mm, "end": v(-19.81, 10.72) * mm});
            skLineSegment(sketch, "E65.0.28", {"start": v(-19.81, 10.72) * mm, "end": v(-18.7, 4.9) * mm});
            skLineSegment(sketch, "E65.0.29", {"start": v(-18.7, 4.9) * mm, "end": v(-13.7, 4.66) * mm});
            skLineSegment(sketch, "E65.0.30", {"start": v(-13.7, 4.66) * mm, "end": v(-13.56, 4.65) * mm});
            skLineSegment(sketch, "E65.0.31", {"start": v(-13.56, 4.65) * mm, "end": v(-13.19, 1.3) * mm});
            skLineSegment(sketch, "E65.0.32", {"start": v(-13.19, 1.3) * mm, "end": v(-13, -0.98) * mm});
            skLineSegment(sketch, "E65.0.33", {"start": v(-13, -0.98) * mm, "end": v(-12.98, -3.47) * mm});
            skLineSegment(sketch, "E65.0.34", {"start": v(-12.98, -3.47) * mm, "end": v(-13.86, -10.75) * mm});
            skLineSegment(sketch, "E65.0.35", {"start": v(-13.86, -10.75) * mm, "end": v(-14.81, -19.6) * mm});
            skLineSegment(sketch, "E65.0.36", {"start": v(-14.81, -19.6) * mm, "end": v(-14.73, -21.77) * mm});
            skLineSegment(sketch, "E65.0.37", {"start": v(-14.73, -21.77) * mm, "end": v(-14.03, -29.33) * mm});
            skLineSegment(sketch, "E65.0.38", {"start": v(-14.03, -29.33) * mm, "end": v(-8.28, -29.1) * mm});
            skLineSegment(sketch, "E65.0.39", {"start": v(-8.28, -29.1) * mm, "end": v(-0.43, -28.8) * mm});
            skLineSegment(sketch, "E65.0.40", {"start": v(-0.43, -28.8) * mm, "end": v(-1.03, -23.45) * mm});
            skLineSegment(sketch, "E65.0.41", {"start": v(-1.03, -23.45) * mm, "end": v(-1.31, -19.45) * mm});
            skLineSegment(sketch, "E65.0.42", {"start": v(-1.31, -19.45) * mm, "end": v(-1.28, -15.72) * mm});
            skLineSegment(sketch, "E65.0.43", {"start": v(-1.28, -15.72) * mm, "end": v(-0.82, -8.77) * mm});
            skLineSegment(sketch, "E65.0.44", {"start": v(-0.82, -8.77) * mm, "end": v(-0.24, -1.7) * mm});
            skLineSegment(sketch, "E66.0", {"start": v(1.17, -8.91) * mm, "end": v(1.76, -1.8) * mm});
            skLineSegment(sketch, "E66.1", {"start": v(0.72, -15.8) * mm, "end": v(1.17, -8.91) * mm});
            skLineSegment(sketch, "E66.2", {"start": v(0.69, -19.39) * mm, "end": v(0.72, -15.8) * mm});
            skLineSegment(sketch, "E66.3", {"start": v(0.97, -23.26) * mm, "end": v(0.69, -19.39) * mm});
            skLineSegment(sketch, "E66.4", {"start": v(1.8, -30.72) * mm, "end": v(0.97, -23.26) * mm});
            skLineSegment(sketch, "E66.5", {"start": v(-8.2, -31.1) * mm, "end": v(1.8, -30.72) * mm});
            skLineSegment(sketch, "E66.6", {"start": v(-15.85, -31.4) * mm, "end": v(-8.2, -31.1) * mm});
            skLineSegment(sketch, "E66.7", {"start": v(-16.73, -21.9) * mm, "end": v(-15.85, -31.4) * mm});
            skLineSegment(sketch, "E66.8", {"start": v(-16.82, -19.54) * mm, "end": v(-16.73, -21.9) * mm});
            skLineSegment(sketch, "E66.9", {"start": v(-15.85, -10.52) * mm, "end": v(-16.82, -19.54) * mm});
            skLineSegment(sketch, "E66.10", {"start": v(-14.98, -3.36) * mm, "end": v(-15.85, -10.52) * mm});
            skLineSegment(sketch, "E66.11", {"start": v(1.76, -1.8) * mm, "end": v(1.8, 0.94) * mm});
            skLineSegment(sketch, "E66.12", {"start": v(-15, -1.07) * mm, "end": v(-14.98, -3.36) * mm});
            skLineSegment(sketch, "E66.13", {"start": v(-15.18, 1.1) * mm, "end": v(-15, -1.07) * mm});
            skLineSegment(sketch, "E66.14", {"start": v(-15.36, 2.74) * mm, "end": v(-15.18, 1.1) * mm});
            skLineSegment(sketch, "E66.15", {"start": v(-20.36, 2.98) * mm, "end": v(-15.36, 2.74) * mm});
            skLineSegment(sketch, "E66.16", {"start": v(-21.82, 10.59) * mm, "end": v(-20.36, 2.98) * mm});
            skLineSegment(sketch, "E66.17", {"start": v(-21.39, 18.53) * mm, "end": v(-21.82, 10.59) * mm});
            skLineSegment(sketch, "E66.18", {"start": v(-20.33, 23.6) * mm, "end": v(-21.39, 18.53) * mm});
            skLineSegment(sketch, "E66.19", {"start": v(-16.46, 23.8) * mm, "end": v(-20.33, 23.6) * mm});
            skLineSegment(sketch, "E66.20", {"start": v(20.6, 19.68) * mm, "end": v(19.38, 23.17) * mm});
            skLineSegment(sketch, "E66.21", {"start": v(21.44, 16.48) * mm, "end": v(20.6, 19.68) * mm});
            skLineSegment(sketch, "E66.22", {"start": v(21.84, 13.16) * mm, "end": v(21.44, 16.48) * mm});
            skLineSegment(sketch, "E66.23", {"start": v(20.47, 6.45) * mm, "end": v(21.84, 13.16) * mm});
            skLineSegment(sketch, "E66.24", {"start": v(18.67, 1.6) * mm, "end": v(20.47, 6.45) * mm});
            skLineSegment(sketch, "E66.25", {"start": v(16.8, -2.75) * mm, "end": v(18.67, 1.6) * mm});
            skLineSegment(sketch, "E66.26", {"start": v(1.8, 0.94) * mm, "end": v(6.14, -0.02) * mm});
            skLineSegment(sketch, "E66.27", {"start": v(6.14, -0.02) * mm, "end": v(8.94, -0.7) * mm});
            skLineSegment(sketch, "E66.28", {"start": v(8.94, -0.7) * mm, "end": v(11.97, -1.48) * mm});
            skLineSegment(sketch, "E66.29", {"start": v(11.97, -1.48) * mm, "end": v(16.8, -2.75) * mm});
            skLineSegment(sketch, "E66.30", {"start": v(19.38, 23.17) * mm, "end": v(18.33, 25.77) * mm});
            skLineSegment(sketch, "E66.31", {"start": v(18.33, 25.77) * mm, "end": v(16.78, 29.28) * mm});
            skLineSegment(sketch, "E66.32", {"start": v(16.78, 29.28) * mm, "end": v(10.7, 27.71) * mm});
            skLineSegment(sketch, "E66.33", {"start": v(10.7, 27.71) * mm, "end": v(7.57, 26.94) * mm});
            skLineSegment(sketch, "E66.34", {"start": v(7.57, 26.94) * mm, "end": v(5.12, 26.36) * mm});
            skLineSegment(sketch, "E66.35", {"start": v(5.12, 26.36) * mm, "end": v(1.04, 25.47) * mm});
            skLineSegment(sketch, "E66.36", {"start": v(1.44, 25.55) * mm, "end": v(1.04, 25.47) * mm});
            skLineSegment(sketch, "E66.37", {"start": v(1.44, 25.55) * mm, "end": v(1.51, 29.02) * mm});
            skLineSegment(sketch, "E66.38", {"start": v(1.51, 29.02) * mm, "end": v(-4.65, 31.13) * mm});
            skLineSegment(sketch, "E66.39", {"start": v(-4.65, 31.13) * mm, "end": v(-10.13, 31.13) * mm});
            skLineSegment(sketch, "E66.40", {"start": v(-10.13, 31.13) * mm, "end": v(-16.46, 31.44) * mm});
            skLineSegment(sketch, "E66.41", {"start": v(-16.46, 31.44) * mm, "end": v(-16.46, 23.8) * mm});
            skSolve(sketch);
        }
        {
            var Q0;
            Q0 = qSketchRegion(id + "F7", true);
            extrude(context, id + "F8", {"entities" : qUnion([Q0]), "operationType" : NewBodyOperationType.ADD, "oppositeDirection" : true, "depth" : 1.6 * mm});
        }
    });
